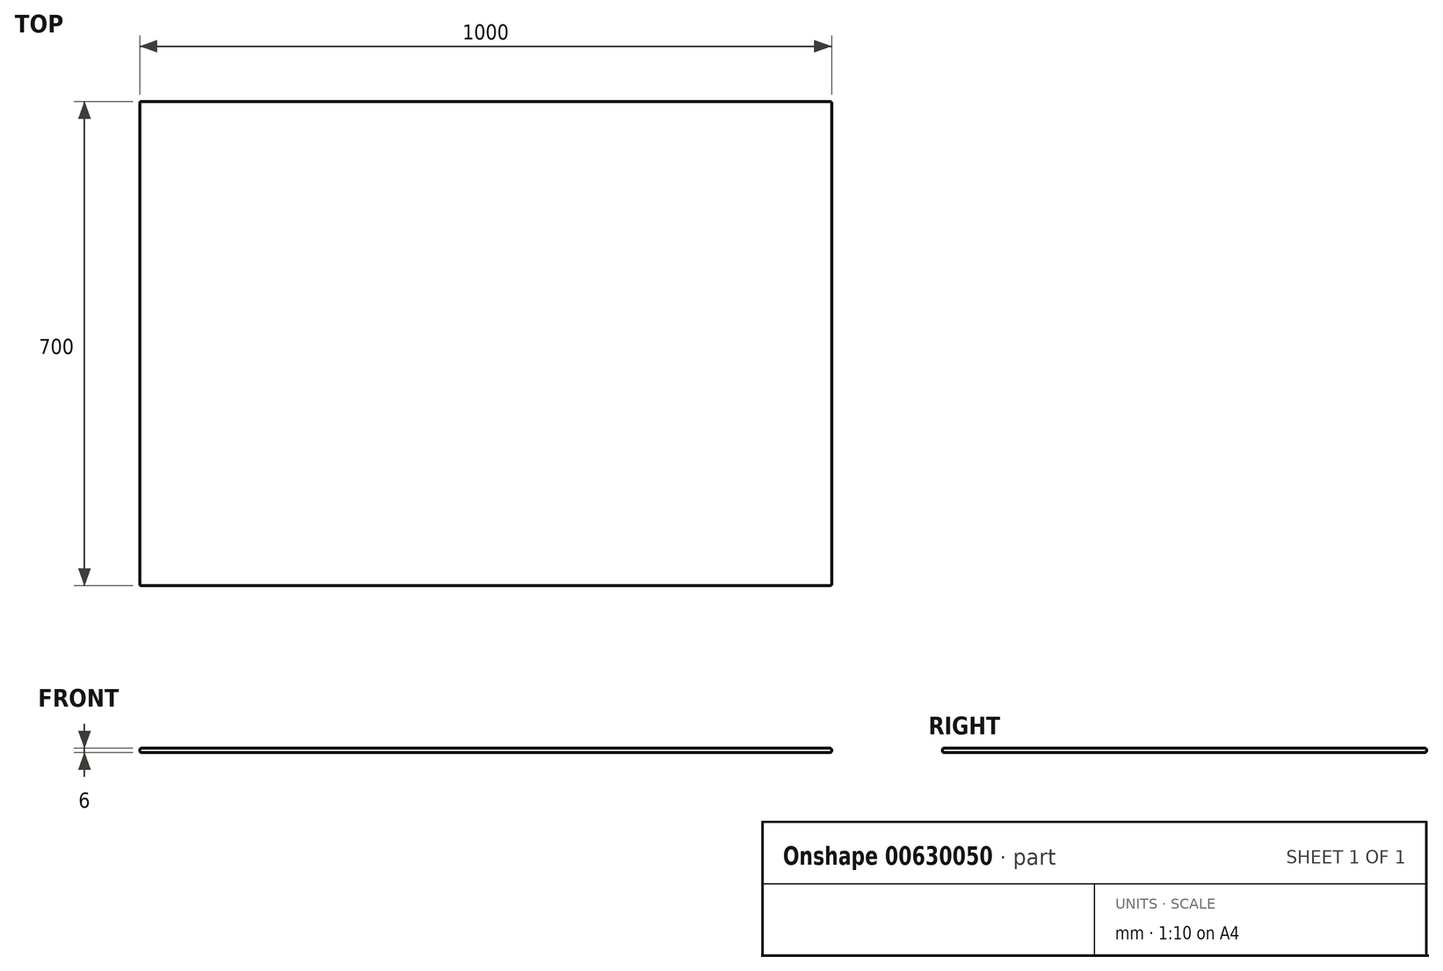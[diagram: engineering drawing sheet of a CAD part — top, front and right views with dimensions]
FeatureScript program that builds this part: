
annotation { "Feature Type Name" : "Feature", "Feature Type Description" : "" }
export const myFeature = defineFeature(function(context is Context, id is Id, definition is map)
    precondition{}
    {
        {
            var Q0;
            Q0=qCreatedBy(makeId("Top.planeOp"),FACE);
            var sketch = newSketch(context, id + "F0", { "sketchPlane" : qUnion([Q0])});
            skLineSegment(sketch, "E0.bottom", {"start": v(0, 0) * mm, "end": v(1000, 0) * mm});
            skLineSegment(sketch, "E0.top", {"start": v(0, 700) * mm, "end": v(1000, 700) * mm});
            skLineSegment(sketch, "E0.left", {"start": v(0, 0) * mm, "end": v(0, 700) * mm});
            skLineSegment(sketch, "E0.right", {"start": v(1000, 0) * mm, "end": v(1000, 700) * mm});
            skSolve(sketch);
        }
        {
            var Q0;
            Q0 = qSketchRegion(id + "F0", true);
            extrude(context, id + "F1", {"entities" : qUnion([Q0]), "depth" : 6 * mm, "offsetDistance" : 25 * mm});
        }
        {
            var Q0;
            Q0=makeQuery(id+"F1.opExtrude","CAP_EDGE",EDGE,{"disambiguationData":[OSD([sQuery(id+"F0.wireOp",EDGE,"E0.right")])],"isStart":true});
            var Q1;
            Q1=makeQuery(id+"F1.opExtrude","CAP_EDGE",EDGE,{"disambiguationData":[OSD([sQuery(id+"F0.wireOp",EDGE,"E0.top")])],"isStart":true});
            var Q2;
            Q2=makeQuery(id+"F1.opExtrude","CAP_EDGE",EDGE,{"disambiguationData":[OSD([sQuery(id+"F0.wireOp",EDGE,"E0.bottom")])],"isStart":false});
            var Q3;
            Q3=makeQuery(id+"F1.opExtrude","CAP_EDGE",EDGE,{"disambiguationData":[OSD([sQuery(id+"F0.wireOp",EDGE,"E0.left")])],"isStart":false});
            fillet(context, id + "F2", {"entities" : qUnion([Q0, Q1, Q2, Q3]), "radius" : 2 * mm, "tangentPropagation" : true, "allowEdgeOverflow" : false});
        }
        {
            var Q0;
            Q0=makeQuery(id+"F1.opExtrude","CAP_EDGE",EDGE,{"disambiguationData":[OSD([sQuery(id+"F0.wireOp",EDGE,"E0.bottom")])],"isStart":true});
            var Q1;
            Q1=makeQuery(id+"F1.opExtrude","CAP_EDGE",EDGE,{"disambiguationData":[OSD([sQuery(id+"F0.wireOp",EDGE,"E0.right")])],"isStart":false});
            var Q2;
            Q2=makeQuery(id+"F1.opExtrude","SWEPT_EDGE",EDGE,{"disambiguationData":[OSD([sQuery(id+"F0.wireOp",EDGE,"E0.bottom"),sQuery(id+"F0.wireOp",EDGE,"E0.right")])]});
            fillet(context, id + "F3", {"entities" : qUnion([Q0, Q1, Q2]), "radius" : 2 * mm, "tangentPropagation" : true, "allowEdgeOverflow" : false});
        }
        {
            var Q0;
            Q0=makeQuery(id+"F1.opExtrude","CAP_EDGE",EDGE,{"disambiguationData":[OSD([sQuery(id+"F0.wireOp",EDGE,"E0.left")])],"isStart":true});
            var Q1;
            Q1=makeQuery(id+"F1.opExtrude","SWEPT_EDGE",EDGE,{"disambiguationData":[OSD([sQuery(id+"F0.wireOp",EDGE,"E0.bottom"),sQuery(id+"F0.wireOp",EDGE,"E0.left")])]});
            fillet(context, id + "F4", {"entities" : qUnion([Q0, Q1]), "radius" : 2 * mm, "tangentPropagation" : true, "allowEdgeOverflow" : false});
        }
    });
